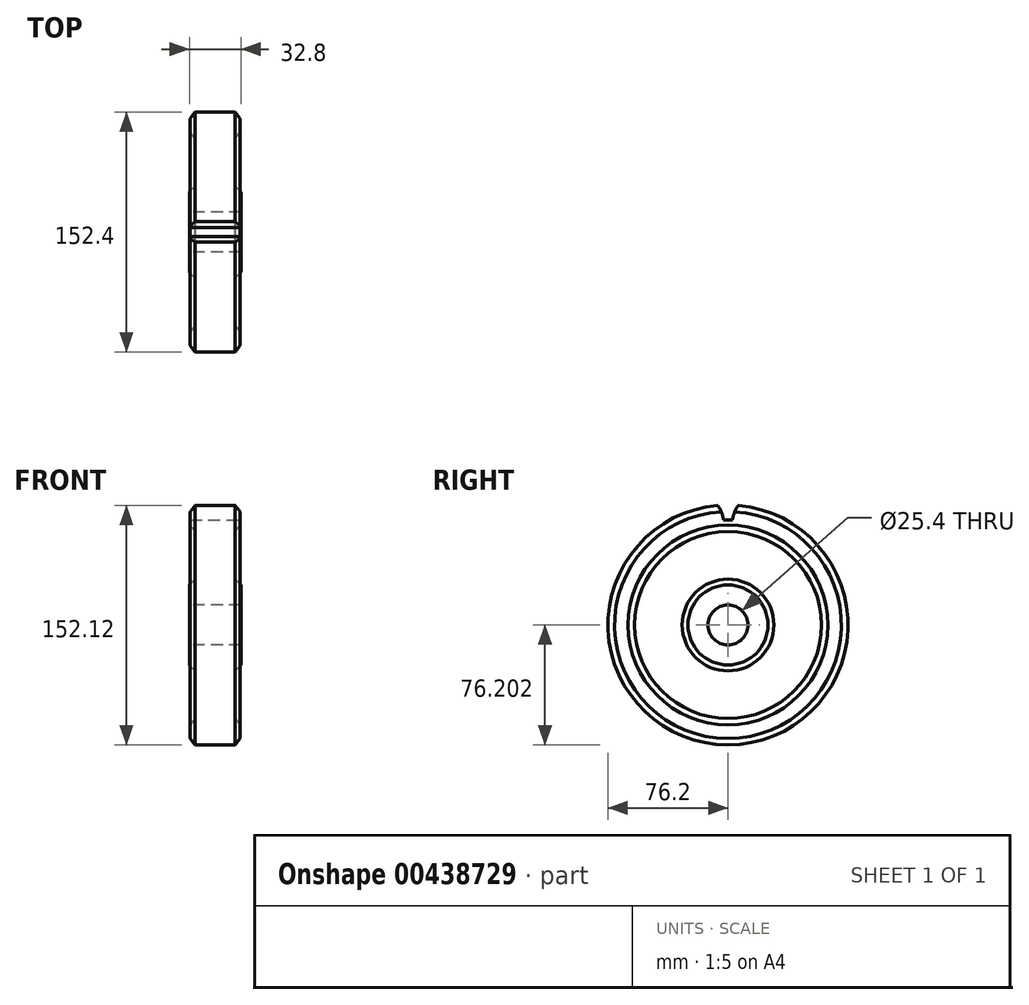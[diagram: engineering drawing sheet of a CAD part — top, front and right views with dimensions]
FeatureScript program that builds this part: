
annotation { "Feature Type Name" : "Feature", "Feature Type Description" : "" }
export const myFeature = defineFeature(function(context is Context, id is Id, definition is map)
    precondition{}
    {
        {
            var Q0;
            Q0=qCreatedBy(makeId("Front.planeOp"),FACE);
            var sketch = newSketch(context, id + "F0", { "sketchPlane" : qUnion([Q0])});
            skLineSegment(sketch, "E0", {"start": v(0, -30.9) * mm, "end": v(0, 32.6) * mm});
            skLineSegment(sketch, "E1", {"start": v(0, 32.6) * mm, "end": v(12.7, 32.6) * mm});
            skLineSegment(sketch, "E2", {"start": v(12.7, 32.6) * mm, "end": v(15.87, 28.44) * mm});
            skLineSegment(sketch, "E3", {"start": v(15.87, 28.44) * mm, "end": v(15.87, 19.9) * mm});
            skLineSegment(sketch, "E4", {"start": v(15.87, 19.9) * mm, "end": v(12.7, 15.74) * mm});
            skLineSegment(sketch, "E5", {"start": v(12.7, 15.74) * mm, "end": v(12.7, -14.5) * mm});
            skLineSegment(sketch, "E6", {"start": v(12.7, -14.5) * mm, "end": v(16.4, -18.2) * mm});
            skLineSegment(sketch, "E7", {"start": v(16.4, -18.2) * mm, "end": v(16.4, -30.9) * mm});
            skLineSegment(sketch, "E8", {"start": v(16.4, -30.9) * mm, "end": v(0, -30.9) * mm});
            skLineSegment(sketch, "E9", {"start": v(0, -30.9) * mm, "end": v(0, -43.6) * mm});
            skLineSegment(sketch, "E10", {"start": v(0, -43.6) * mm, "end": v(11.4, -43.6) * mm});
            skLineSegment(sketch, "E11.MirrorCS", {"start": v(0, 32.6) * mm, "end": v(-12.7, 32.6) * mm});
            skLineSegment(sketch, "E12.MirrorCS", {"start": v(-12.7, 32.6) * mm, "end": v(-15.88, 28.44) * mm});
            skLineSegment(sketch, "E13.MirrorCS", {"start": v(-15.88, 28.44) * mm, "end": v(-15.88, 19.9) * mm});
            skLineSegment(sketch, "E14.MirrorCS", {"start": v(-15.88, 19.9) * mm, "end": v(-12.7, 15.74) * mm});
            skLineSegment(sketch, "E15.MirrorCS", {"start": v(-12.7, 15.74) * mm, "end": v(-12.7, -14.5) * mm});
            skLineSegment(sketch, "E16.MirrorCS", {"start": v(-12.7, -14.5) * mm, "end": v(-16.4, -18.2) * mm});
            skLineSegment(sketch, "E17.MirrorCS", {"start": v(-16.4, -18.2) * mm, "end": v(-16.4, -30.9) * mm});
            skLineSegment(sketch, "E18.MirrorCS", {"start": v(-16.4, -30.9) * mm, "end": v(0, -30.9) * mm});
            skSolve(sketch);
        }
        {
            var Q0;
            Q0=makeQuery(id+"F0.imprint","IMPRINT",FACE,{"disambiguationData":[TD([[makeQuery(id+"F0.imprint","IMPRINT",EDGE,{"derivedFrom":sQuery(id+"F0.wireOp",EDGE,"E0")}),1.0]])]});
            var Q1;
            Q1=makeQuery(id+"F0.imprint","IMPRINT",FACE,{"disambiguationData":[TD([[makeQuery(id+"F0.imprint","IMPRINT",EDGE,{"derivedFrom":sQuery(id+"F0.wireOp",EDGE,"E0")}),-1.0]])]});
            var Q2;
            Q2=sQuery(id+"F0.wireOp",EDGE,"E10");
            revolve(context, id + "F1", {"entities" : qUnion([Q0, Q1]), "axis" : qUnion([Q2]), "revolveType" : RevolveType.FULL});
        }
        {
            var Q0;
            Q0=makeQuery(id+"F1.opRevolve","SWEPT_FACE",FACE,{"disambiguationData":[OSD([sQuery(id+"F0.wireOp",EDGE,"E3")])]});
            var sketch = newSketch(context, id + "F2", { "sketchPlane" : qUnion([Q0])});
            skLineSegment(sketch, "E19", {"start": v(0, -43.6) * mm, "end": v(0, 66.59) * mm});
            skLineSegment(sketch, "E20", {"start": v(0, 23.08) * mm, "end": v(2.86, 23.08) * mm});
            skArc(sketch, "E21", {"start": v(6.54, 32.32) * mm, "mid": v(4.08, 27.94) * mm, "end": v(2.86, 23.08) * mm});
            skArc(sketch, "E22.0", {"start": v(6.54, 32.32) * mm, "mid": v(0, 32.6) * mm, "end": v(-6.54, 32.32) * mm});
            skLineSegment(sketch, "E23.MirrorCS", {"start": v(0, 23.08) * mm, "end": v(-2.86, 23.08) * mm});
            skArc(sketch, "E24.MirrorCS", {"start": v(-6.54, 32.32) * mm, "mid": v(-4.08, 27.94) * mm, "end": v(-2.86, 23.08) * mm});
            skSolve(sketch);
        }
        {
            var Q0;
            {var subQ0=sQuery(id+"F2.wireOp",EDGE,"E22.0");var subQ5=sQuery(id+"F2.wireOp",EDGE,"E24.MirrorCS");var subQ6=makeQuery(id+"F2.imprint","INTERSECT",VERTEX,{"derivedFrom":[subQ0,subQ5]});Q0=makeQuery(id+"F2.imprint","IMPRINT",FACE,{"disambiguationData":[TD([[makeQuery(id+"F2.imprint","IMPRINT",EDGE,{"disambiguationData":[TD([[subQ6,1.0]])],"derivedFrom":subQ0}),1.0]])]});}
            var Q1;
            {var subQ0=sQuery(id+"F2.wireOp",EDGE,"E23.MirrorCS");Q1=makeQuery(id+"F2.imprint","IMPRINT",FACE,{"disambiguationData":[TD([[makeQuery(id+"F2.imprint","IMPRINT",EDGE,{"derivedFrom":subQ0}),-1.0]])]});}
            var Q2;
            {var subQ0=sQuery(id+"F2.wireOp",EDGE,"E20");Q2=makeQuery(id+"F2.imprint","IMPRINT",FACE,{"disambiguationData":[TD([[makeQuery(id+"F2.imprint","IMPRINT",EDGE,{"derivedFrom":subQ0}),1.0]])]});}
            var Q3;
            {var subQ0=sQuery(id+"F2.wireOp",EDGE,"E22.0");var subQ5=sQuery(id+"F2.wireOp",EDGE,"E21");var subQ6=makeQuery(id+"F2.imprint","INTERSECT",VERTEX,{"derivedFrom":[subQ5,subQ0]});Q3=makeQuery(id+"F2.imprint","IMPRINT",FACE,{"disambiguationData":[TD([[makeQuery(id+"F2.imprint","IMPRINT",EDGE,{"disambiguationData":[TD([[subQ6,-1.0]])],"derivedFrom":subQ0}),1.0]])]});}
            extrude(context, id + "F3", {"entities" : qUnion([Q0, Q1, Q2, Q3]), "operationType" : NewBodyOperationType.REMOVE, "endBound" : BoundingType.THROUGH_ALL, "oppositeDirection" : true, "depth" : 25.4 * mm});
        }
    });
